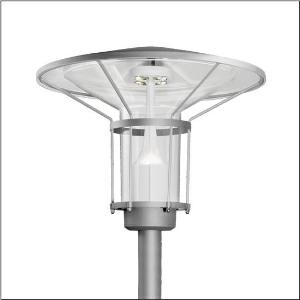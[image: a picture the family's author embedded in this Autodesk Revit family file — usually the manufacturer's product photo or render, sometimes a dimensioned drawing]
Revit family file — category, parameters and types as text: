
# Revit family: laterne_classic_iq___p1_0a_5xa5245bf14hp_df6d
name_source: partatom
category: Lighting Fixtures
units: mm (PartAtom-declared; Revit-internal decimal feet)

## family parameters
Cut with Voids When Loaded = No
Host = Face
Light Source = No
Part Type = Normal
Room Calculation Point = No
Round Connector Dimension = Use Diameter
Shared = No

## types (1)
- --- (1 x LED, 3480 lm, 33.6 W, 2200K)
    Apparent Load = 34 VA
    CIE Flux Codes = 31 61 91 96 100
    Color Rendering = 70
    Color Temperature = 2200K
    Default Elevation = 1800 mm
    Description = Lantern Classic iQ, mast luminaire, Module 540 iQ-SR, primary light control with 3 zone facetted reflector, of plastic, silver coated, highly specular, structured, primary optical cover: cover, of PMMA, transparent, light distribution: P1.0a, light emission: direct distribution, primary light characteristic: strongly asymmetric, installation type: post-top, LED, High Power LED, rated luminous flux: 3.480lm, luminous efficacy: 104lm/W, light colour: 722, colour temperature: 2200K, control gear: ECG iQ, control: pre-setting: logarithmic dimming characteristic, Street-Remote, Auto-Match, Temp-Guard, Lumen-Switch, Night-Set, Smart-Wire, Light-Fading, Desk-Remote (wireless, voltage-free reading and setting of iQ features in the workshop via application-optimized NFC function/RFID function), optimised constant luminous flux control (CLO 2.0), with terminal, 6-pole, max. 2.5mm², mains connection: 230..240V, AC, 50/60Hz, start of lifetime: 34W, end of service life: 36W, reduction: 15W, luminaire housing, upper part, of glass-fibre reinforced polyester, coated, Siteco® metallic grey (DB 702S), diameter: 750mm, height: 596mm, spigot size: d x l = 76 x 70mm (post-top) | with reducer (optional accessory) 60 x 70mm, post-top mast mounting element, of diecast aluminium, coated, Siteco® metallic grey (DB 702S), Module 540 iQ-SR, traffic white (RAL 9016), equipment: Power, protection rating (complete): IP65, insulation class (complete): insulation class II (safety insulation), certification: CE, ENEC, VDE, packaging unit: 1 piece

Light Distribution: P1.0a
    Height = 596 mm
    Lamp = 1 x LED
    Lamp Light Flux = 3480 lm
    Lamp Power = 33.6 W
    Lamp count = 1
    Length = 750 mm
    Luminous efficacy = 104 lm/W
    Manufacturer = Siteco
    ModVariant = No
    Model = 5XA5245BF14HP
    Number of Poles = 1
    OnlyDefault = Yes
    Power Factor = 1
    Product Name = Laterne Classic iQ | P1.0a
    Product group = mast luminaire | pylon top
    ProductGroupID = 6100
    Protection Class = Protection class II
    Protection Degree = IP 65
    RLX_Detail_Level = 1
    RLX_Emergency_Light_Flux = 0 lm
    RLX_Emergency_Type = 0
    RLX_Emergency_Type_DB = No
    RlxData = <blob elided: 65329 chars, md5=84f53626>
    Socket = socket
    Standby Power = 0 W
    System Light Flux = 3480 lm
    System Power = 34 W
    Type Comments = factory setting: luminous flux: 100 % | dim-lin: 254 | 695 mA
    Type Image = l_1006052.jpg
    URL = http://relux.com
    VarID = @adj_165887
    Voltage = 0 V
    Weight = 0.00 kg
    Width = 0 mm  [stored 0 ft]

note: [stored X ft] marks values corroborated as IEEE doubles in the binary element streams (Revit-internal decimal feet)

## geometry (parser evidence)
native form markers: Blend x4, Sweep x11
no freeform markers — native parametric forms only
